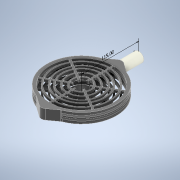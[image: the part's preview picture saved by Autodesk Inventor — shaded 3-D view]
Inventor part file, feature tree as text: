
AUTODESK INVENTOR PART (.ipt)
format: ipt  version: 2021 (Build 250183000, 183)  size: 593,408 bytes
history: native  units: mm
features: extrude x9, sketch x9, other x3, fillet x2, plane x2
ambient origin geometry x8: Origin, YZ Plane, XZ Plane, XY Plane, X Axis, Y Axis, Z Axis, Center Point
bodies: Solid1 (feature_tree)
feature tree (25):
  other  "Annotations"
  extrude  "Extrusion1"  Depth=140.0mm
  extrude  "Extrusion2"  Depth=55.0mm
  fillet  "Fillet1"  Radius=60.0mm
  fillet  "Fillet2"  Radius=75.0mm
  extrude  "Extrusion3"  Depth=90.0mm
  extrude  "Extrusion4"  Depth=110.0mm
  extrude  "Extrusion5"  Depth=5.0mm
  plane  "Work Plane1"
  extrude  "Extrusion6"  Depth=10.0mm
  extrude  "Extrusion7"  Depth=30.0mm TaperAngle=360.0deg
  extrude  "Extrusion8"  Depth=50.0mm
  plane  "Work Plane2"
  extrude  "Extrusion9"  Depth=10.0mm TaperAngle=360.0deg
  sketch  "Sketch1"  dims[d0=128.0mm d1=140.0mm]
  sketch  "Sketch2"  dims[d2=40.0mm d3=55.0mm d4=60.0mm d5=75.0mm]
  sketch  "Sketch3"  dims[d6=80.0mm d7=90.0mm]
  sketch  "Sketch4"  dims[d8=95.0mm d9=110.0mm]
  sketch  "Sketch5"  dims[d10=115.0mm d11=5.0mm]
  sketch  "Sketch7"  dims[d12=10.0mm d13=67.0mm]
  sketch  "Sketch8"  dims[d14=0.0mm d15=30.0mm d17=360.0deg]
  sketch  "Sketch9"  dims[d19=5.0mm d20=0.0mm d21=50.0mm]
  sketch  "Sketch10"  dims[d23=18.0mm d24=20.0mm d26=360.0deg d28=15.0mm d29=0.0mm d30=10.0mm d31=10.0mm d32=5.0mm d33=2.0mm d34=0.0mm d35=25.0mm d36=30.0mm d37=0.0mm d38=18.0mm d39=10.0mm d40=0.0mm d41=5.0mm d42=0.0mm d43=5.0mm d44=140.0mm d45=128.0mm d46=3.0mm d47=0.0mm d49=60.0mm d50=128.0mm d51=140.0mm d52=40.0mm d53=55.0mm d54=60.0mm d55=75.0mm d56=80.0mm d57=90.0mm d58=95.0mm d59=110.0mm d60=115.0mm d61=1.5mm d62=3.0mm d63=67.0mm d64=0.0mm d65=360.0deg d66=0.0mm d67=5.0mm d68=0.0mm d69=25.0mm d70=5.0mm d71=0.0mm d72=35.0mm d73=-75.0mm d74=20.0mm d75=10.0mm d76=23.957065mm d77=40.0mm d78=0.0mm d79=3.0mm d81=115.0mm]
  other  "Linear Dimension 1"
  other  "Linear Dimension 2"
